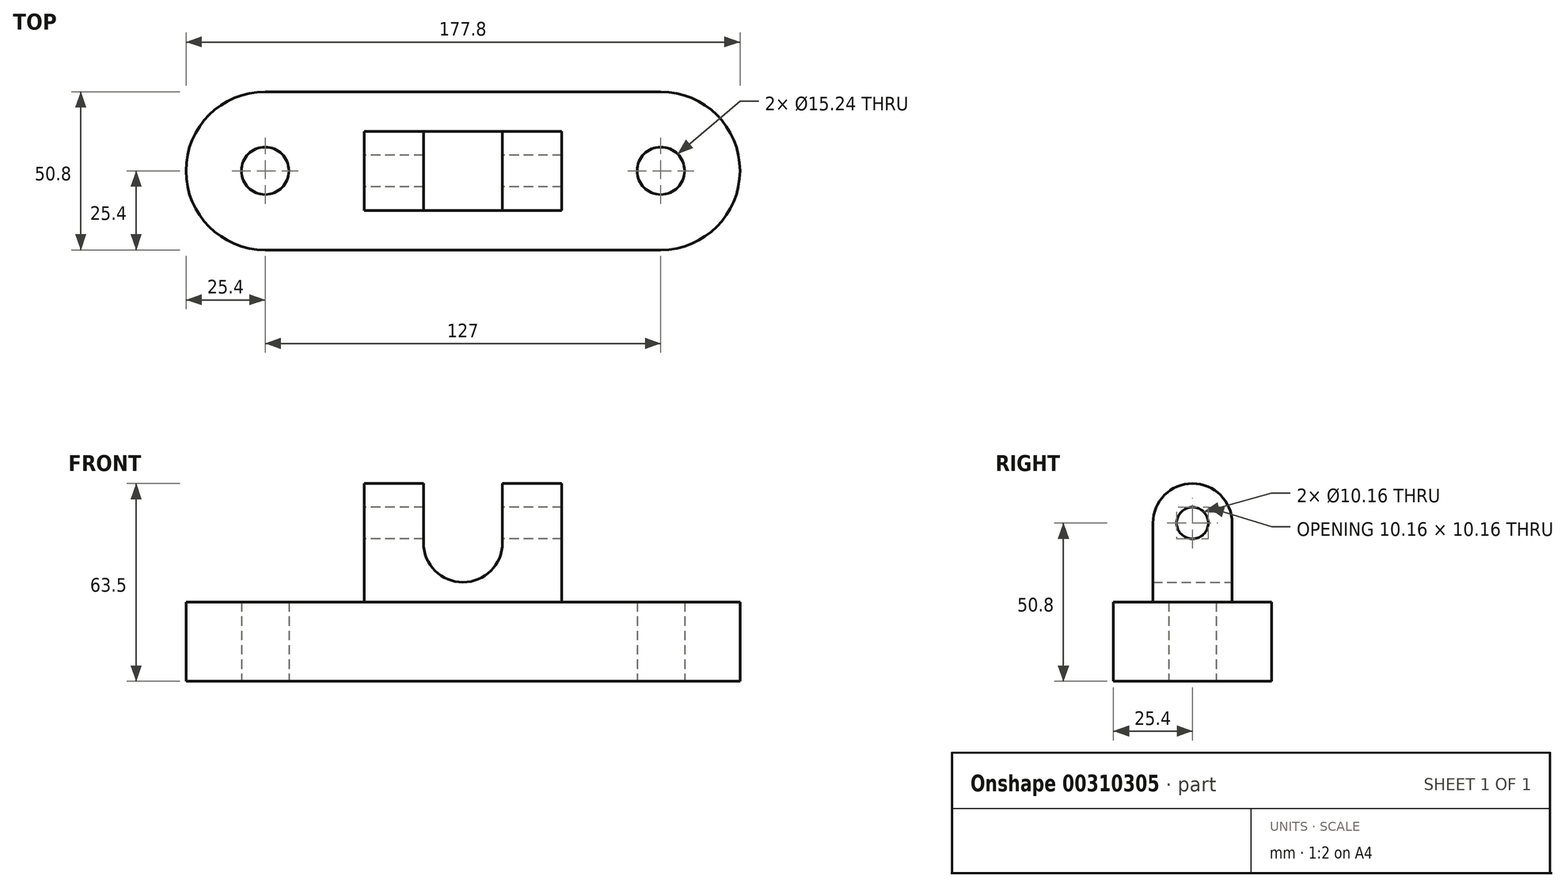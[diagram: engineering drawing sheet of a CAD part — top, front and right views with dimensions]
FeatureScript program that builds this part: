
annotation { "Feature Type Name" : "Feature", "Feature Type Description" : "" }
export const myFeature = defineFeature(function(context is Context, id is Id, definition is map)
    precondition{}
    {
        {
            var Q0;
            Q0=qCreatedBy(makeId("Top.planeOp"),FACE);
            var sketch = newSketch(context, id + "F0", { "sketchPlane" : qUnion([Q0])});
            skArc(sketch, "E0", {"start": v(-63.5, 25.4) * mm, "mid": v(-88.9, 0) * mm, "end": v(-63.5, -25.4) * mm});
            skArc(sketch, "E1", {"start": v(63.5, -25.4) * mm, "mid": v(88.9, 0) * mm, "end": v(63.5, 25.4) * mm});
            skLineSegment(sketch, "E2", {"start": v(-63.5, 25.4) * mm, "end": v(63.5, 25.4) * mm});
            skLineSegment(sketch, "E3", {"start": v(-63.5, -25.4) * mm, "end": v(63.5, -25.4) * mm});
            skCircle(sketch, "E4", {"center": v(-63.5, 0) * mm, "radius": 7.62 * mm});
            skCircle(sketch, "E5", {"center": v(63.5, 0) * mm, "radius": 7.62 * mm});
            skSolve(sketch);
        }
        {
            var Q0;
            Q0=makeQuery(id+"F0.imprint","IMPRINT",FACE,{"disambiguationData":[TD([[makeQuery(id+"F0.imprint","IMPRINT",EDGE,{"derivedFrom":sQuery(id+"F0.wireOp",EDGE,"E0")}),1.0]])]});
            extrude(context, id + "F1", {"entities" : qUnion([Q0]), "depth" : 25.4 * mm});
        }
        {
            var Q0;
            Q0=qCreatedBy(makeId("Right.planeOp"),FACE);
            var sketch = newSketch(context, id + "F2", { "sketchPlane" : qUnion([Q0])});
            skLineSegment(sketch, "E6.0", {"start": v(-25.4, 25.4) * mm, "end": v(25.4, 25.4) * mm});
            skPoint(sketch, "E6.1", {"position": v(0, 25.4) * mm});
            skLineSegment(sketch, "E7", {"start": v(-12.7, 25.4) * mm, "end": v(-12.7, 50.8) * mm});
            skLineSegment(sketch, "E8", {"start": v(12.7, 25.4) * mm, "end": v(12.7, 50.8) * mm});
            skArc(sketch, "E9", {"start": v(12.7, 50.8) * mm, "mid": v(0, 63.5) * mm, "end": v(-12.7, 50.8) * mm});
            skCircle(sketch, "E10", {"center": v(0, 50.8) * mm, "radius": 5.08 * mm});
            skSolve(sketch);
        }
        {
            var Q0;
            {var subQ1=sQuery(id+"F2.wireOp",EDGE,"E7");Q0=makeQuery(id+"F2.imprint","IMPRINT",FACE,{"disambiguationData":[TD([[makeQuery(id+"F2.imprint","IMPRINT",EDGE,{"derivedFrom":subQ1}),-1.0]])]});}
            extrude(context, id + "F3", {"entities" : qUnion([Q0]), "endBound" : BoundingType.SYMMETRIC, "depth" : 63.5 * mm});
        }
        {
            var Q0;
            Q0=makeQuery(id+"F3.opExtrude","SWEPT_FACE",FACE,{"disambiguationData":[OSD([sQuery(id+"F2.wireOp",EDGE,"E8")])]});
            var sketch = newSketch(context, id + "F4", { "sketchPlane" : qUnion([Q0])});
            skLineSegment(sketch, "E11.0", {"start": v(63.5, 25.4) * mm, "end": v(-63.5, 25.4) * mm});
            skLineSegment(sketch, "E12", {"start": v(-12.7, 44.49) * mm, "end": v(-12.7, 67.75) * mm});
            skLineSegment(sketch, "E13.0.0", {"start": v(31.75, 50.8) * mm, "end": v(31.75, 63.5) * mm});
            skLineSegment(sketch, "E13.0.1", {"start": v(31.75, 50.8) * mm, "end": v(-31.75, 50.8) * mm});
            skLineSegment(sketch, "E13.0.2", {"start": v(-31.75, 50.8) * mm, "end": v(-31.75, 63.5) * mm});
            skLineSegment(sketch, "E13.0.3", {"start": v(-31.75, 50.8) * mm, "end": v(31.75, 50.8) * mm});
            skLineSegment(sketch, "E14", {"start": v(12.7, 44.49) * mm, "end": v(12.7, 67.75) * mm});
            skLineSegment(sketch, "E15", {"start": v(-12.7, 67.75) * mm, "end": v(12.7, 67.75) * mm});
            skArc(sketch, "E16", {"start": v(-12.7, 44.49) * mm, "mid": v(0, 31.79) * mm, "end": v(12.7, 44.49) * mm});
            skSolve(sketch);
        }
        {
            var Q0;
            Q0 = qSketchRegion(id + "F4", true);
            extrude(context, id + "F5", {"entities" : qUnion([Q0]), "operationType" : NewBodyOperationType.REMOVE, "oppositeDirection" : true, "depth" : 25.4 * mm});
        }
    });
